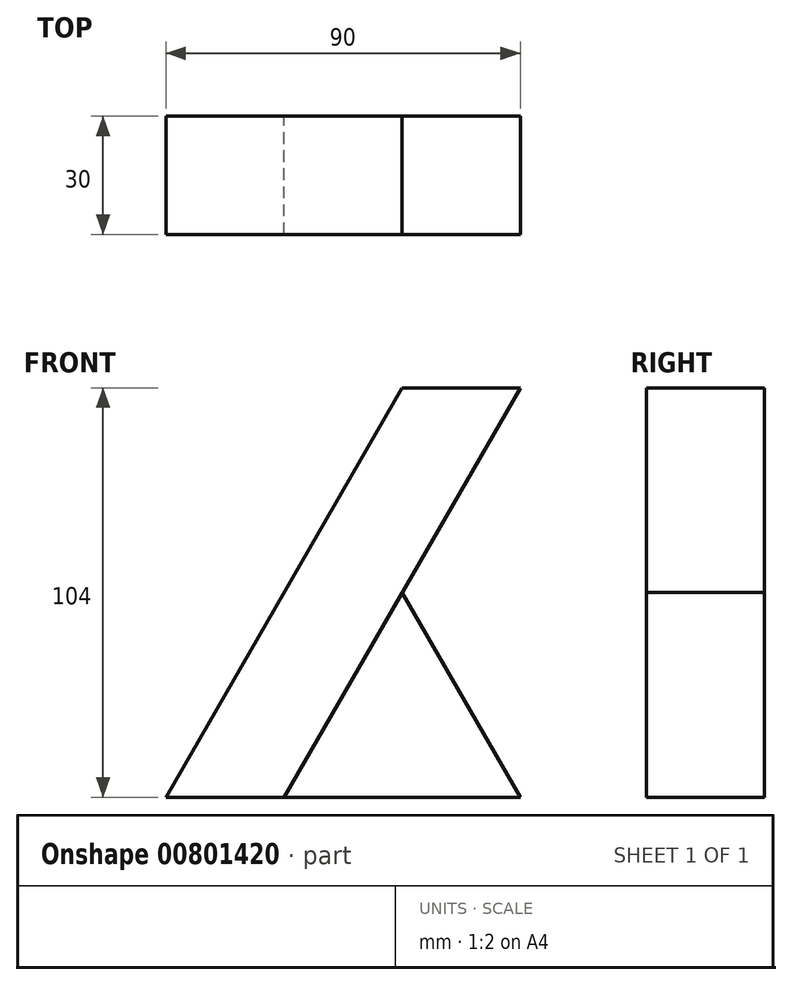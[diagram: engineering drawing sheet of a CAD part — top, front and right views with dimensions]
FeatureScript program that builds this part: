
annotation { "Feature Type Name" : "Feature", "Feature Type Description" : "" }
export const myFeature = defineFeature(function(context is Context, id is Id, definition is map)
    precondition{}
    {
        {
            var Q0;
            Q0=qCreatedBy(makeId("Front.planeOp"),FACE);
            var sketch = newSketch(context, id + "F0", { "sketchPlane" : qUnion([Q0])});
            skLineSegment(sketch, "E0", {"start": v(0, 0) * mm, "end": v(30, 0) * mm});
            skLineSegment(sketch, "E1", {"start": v(30, 0) * mm, "end": v(90, 0) * mm});
            skLineSegment(sketch, "E2", {"start": v(90, 0) * mm, "end": v(60, 51.96) * mm});
            skLineSegment(sketch, "E3", {"start": v(60, 51.96) * mm, "end": v(30, 0) * mm});
            skSolve(sketch);
        }
        {
            var Q0;
            Q0=makeQuery(id+"F0.imprint","IMPRINT",FACE,{"disambiguationData":[TD([[makeQuery(id+"F0.imprint","IMPRINT",EDGE,{"derivedFrom":sQuery(id+"F0.wireOp",EDGE,"E1")}),1.0]])]});
            extrude(context, id + "F1", {"entities" : qUnion([Q0]), "oppositeDirection" : true, "depth" : 30 * mm, "offsetDistance" : 25 * mm});
        }
        {
            var Q0;
            Q0=qCreatedBy(makeId("Top.planeOp"),FACE);
            var sketch = newSketch(context, id + "F2", { "sketchPlane" : qUnion([Q0])});
            skLineSegment(sketch, "E4.0", {"start": v(60, 0) * mm, "end": v(30, 0) * mm});
            skLineSegment(sketch, "E5.0", {"start": v(0, 0) * mm, "end": v(30, 0) * mm});
            skLineSegment(sketch, "E6", {"start": v(30, 0) * mm, "end": v(30, 30) * mm});
            skLineSegment(sketch, "E7", {"start": v(30, 30) * mm, "end": v(0, 30) * mm});
            skLineSegment(sketch, "E8", {"start": v(0, 30) * mm, "end": v(0, 0) * mm});
            skSolve(sketch);
        }
        {
            var Q0;
            Q0=qCreatedBy(makeId("Top.planeOp"),FACE);
            cPlane(context, id + "F3", {"entities" : qUnion([Q0]), "cplaneType" : CPlaneType.OFFSET, "offset" : 104 * mm, "width" : 150 * mm, "height" : 150 * mm});
        }
        {
            var Q0;
            Q0=qCreatedBy(id+"F3.planeOp",FACE);
            var sketch = newSketch(context, id + "F4", { "sketchPlane" : qUnion([Q0])});
            skLineSegment(sketch, "E9.0", {"start": v(0, 0) * mm, "end": v(30, 0) * mm});
            skLineSegment(sketch, "E10.0", {"start": v(60, 0) * mm, "end": v(30, 0) * mm});
            skLineSegment(sketch, "E11.0", {"start": v(90, 0) * mm, "end": v(60, 0) * mm});
            skLineSegment(sketch, "E12", {"start": v(60, 0) * mm, "end": v(60, 30) * mm});
            skLineSegment(sketch, "E13", {"start": v(60, 30) * mm, "end": v(90, 30) * mm});
            skLineSegment(sketch, "E14", {"start": v(90, 30) * mm, "end": v(90, 0) * mm});
            skSolve(sketch);
        }
        {
            var Q0;
            Q0=makeQuery(id+"F2.imprint","IMPRINT",FACE,{"disambiguationData":[TD([[makeQuery(id+"F2.imprint","IMPRINT",EDGE,{"derivedFrom":sQuery(id+"F2.wireOp",EDGE,"E5.0")}),1.0]])]});
            var Q1;
            Q1=makeQuery(id+"F4.imprint","IMPRINT",FACE,{"disambiguationData":[TD([[makeQuery(id+"F4.imprint","IMPRINT",EDGE,{"derivedFrom":sQuery(id+"F4.wireOp",EDGE,"E11.0")}),-1.0]])]});
            loft(context, id + "F5", {"sheetProfilesArray" : [{ "sheetProfileEntities" : qUnion([Q0]) }, { "sheetProfileEntities" : qUnion([Q1]) }]});
        }
    });
